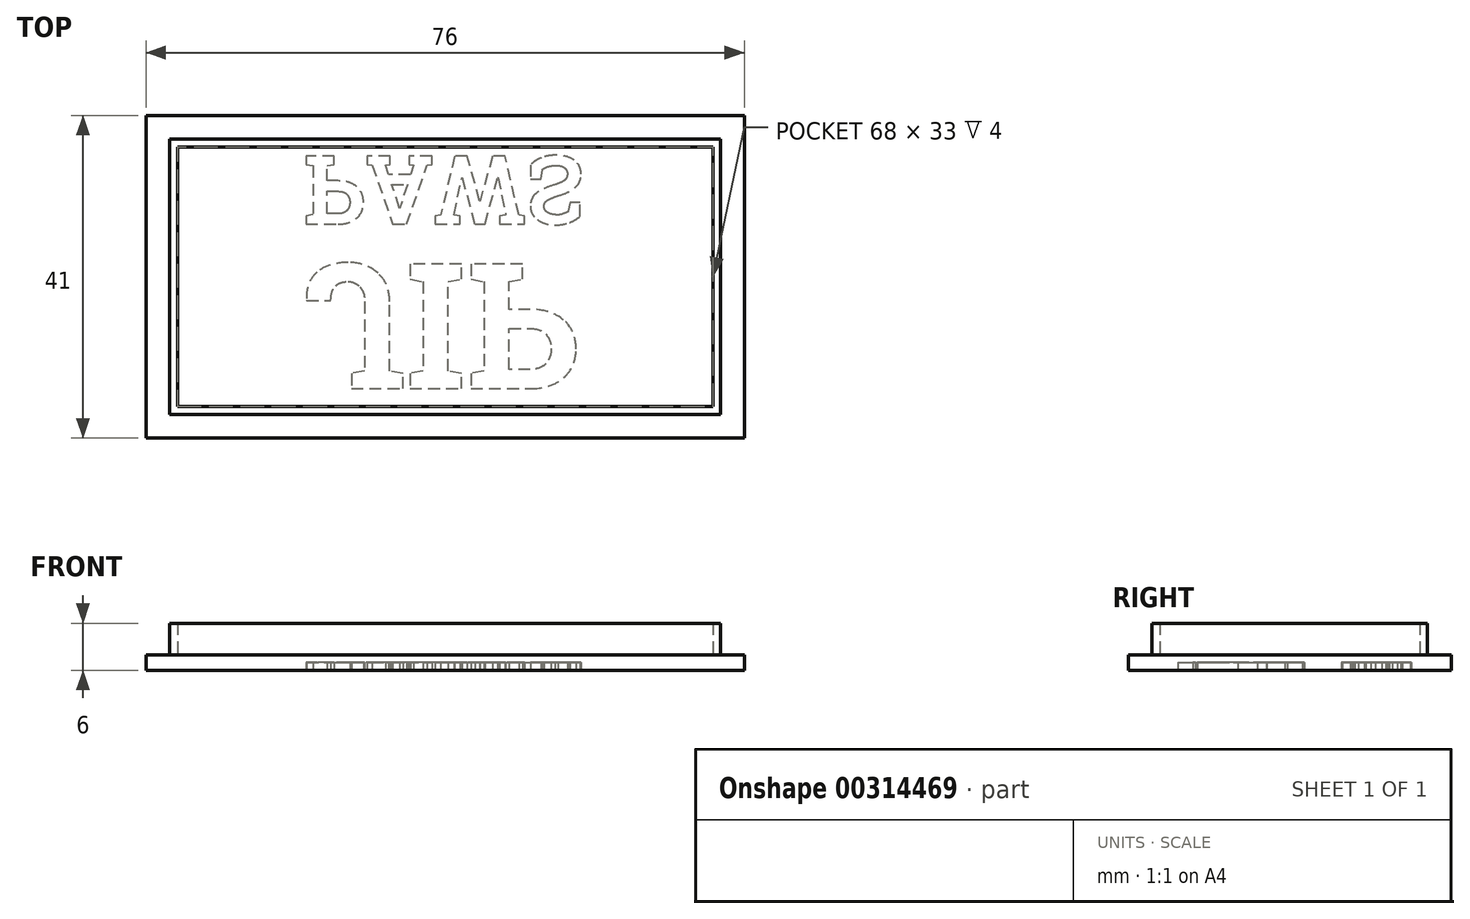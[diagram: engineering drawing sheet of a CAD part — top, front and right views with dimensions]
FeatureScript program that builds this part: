
annotation { "Feature Type Name" : "Feature", "Feature Type Description" : "" }
export const myFeature = defineFeature(function(context is Context, id is Id, definition is map)
    precondition{}
    {
        {
            var Q0;
            Q0=qCreatedBy(makeId("Top.planeOp"),FACE);
            var sketch = newSketch(context, id + "F0", { "sketchPlane" : qUnion([Q0])});
            skLineSegment(sketch, "E0.bottom", {"start": v(0, 0) * mm, "end": v(76, 0) * mm});
            skLineSegment(sketch, "E0.top", {"start": v(0, -41) * mm, "end": v(76, -41) * mm});
            skLineSegment(sketch, "E0.left", {"start": v(0, 0) * mm, "end": v(0, -41) * mm});
            skLineSegment(sketch, "E0.right", {"start": v(76, 0) * mm, "end": v(76, -41) * mm});
            skSolve(sketch);
        }
        {
            var Q0;
            Q0=qSketchRegion(id+"F0",true);
            extrude(context, id + "F1", {"entities" : qUnion([Q0]), "depth" : 2 * mm});
        }
        {
            var Q0;
            Q0=makeQuery(id+"F1.opExtrude","CAP_FACE",FACE,{"disambiguationData":[OSD([sQuery(id+"F0.wireOp",EDGE,"E0.bottom"),sQuery(id+"F0.wireOp",EDGE,"E0.top"),sQuery(id+"F0.wireOp",EDGE,"E0.left"),sQuery(id+"F0.wireOp",EDGE,"E0.right")])],"isStart":false});
            var sketch = newSketch(context, id + "F2", { "sketchPlane" : qUnion([Q0])});
            skLineSegment(sketch, "E1.bottom", {"start": v(3, -3) * mm, "end": v(73, -3) * mm});
            skLineSegment(sketch, "E1.top", {"start": v(3, -38) * mm, "end": v(73, -38) * mm});
            skLineSegment(sketch, "E1.left", {"start": v(3, -3) * mm, "end": v(3, -38) * mm});
            skLineSegment(sketch, "E1.right", {"start": v(73, -3) * mm, "end": v(73, -38) * mm});
            skLineSegment(sketch, "E2.bottom", {"start": v(4, -4) * mm, "end": v(72, -4) * mm});
            skLineSegment(sketch, "E2.top", {"start": v(4, -37) * mm, "end": v(72, -37) * mm});
            skLineSegment(sketch, "E2.left", {"start": v(4, -4) * mm, "end": v(4, -37) * mm});
            skLineSegment(sketch, "E2.right", {"start": v(72, -4) * mm, "end": v(72, -37) * mm});
            skSolve(sketch);
        }
        {
            var Q0;
            Q0=qSketchRegion(id+"F2",true);
            extrude(context, id + "F3", {"entities" : qUnion([Q0]), "operationType" : NewBodyOperationType.ADD, "depth" : 4 * mm});
        }
        {
            var Q0;
            Q0=makeQuery(id+"F1.opExtrude","CAP_FACE",FACE,{"disambiguationData":[OSD([sQuery(id+"F0.wireOp",EDGE,"E0.bottom"),sQuery(id+"F0.wireOp",EDGE,"E0.top"),sQuery(id+"F0.wireOp",EDGE,"E0.left"),sQuery(id+"F0.wireOp",EDGE,"E0.right")])],"isStart":true});
            var sketch = newSketch(context, id + "F4", { "sketchPlane" : qUnion([Q0])});
            skText(sketch, "E3", { "text": "JIP", "fontName": "RobotoSlab-Bold.ttf"});
            skText(sketch, "E4", { "text": "PAWS", "fontName": "RobotoSlab-Bold.ttf"});
            const initialGuessF4  = {"E3": [0.02, 0.0189, 1, 0, 0.016], "E4": [0.02, 0.00517, 1, 0, 0.00874]};
            skSetInitialGuess(sketch, initialGuessF4);
            skSolve(sketch);
        }
        {
            var Q0;
            Q0=qSketchRegion(id+"F4",true);
            extrude(context, id + "F5", {"entities" : qUnion([Q0]), "operationType" : NewBodyOperationType.REMOVE, "oppositeDirection" : true, "depth" : 1 * mm});
        }
    });
